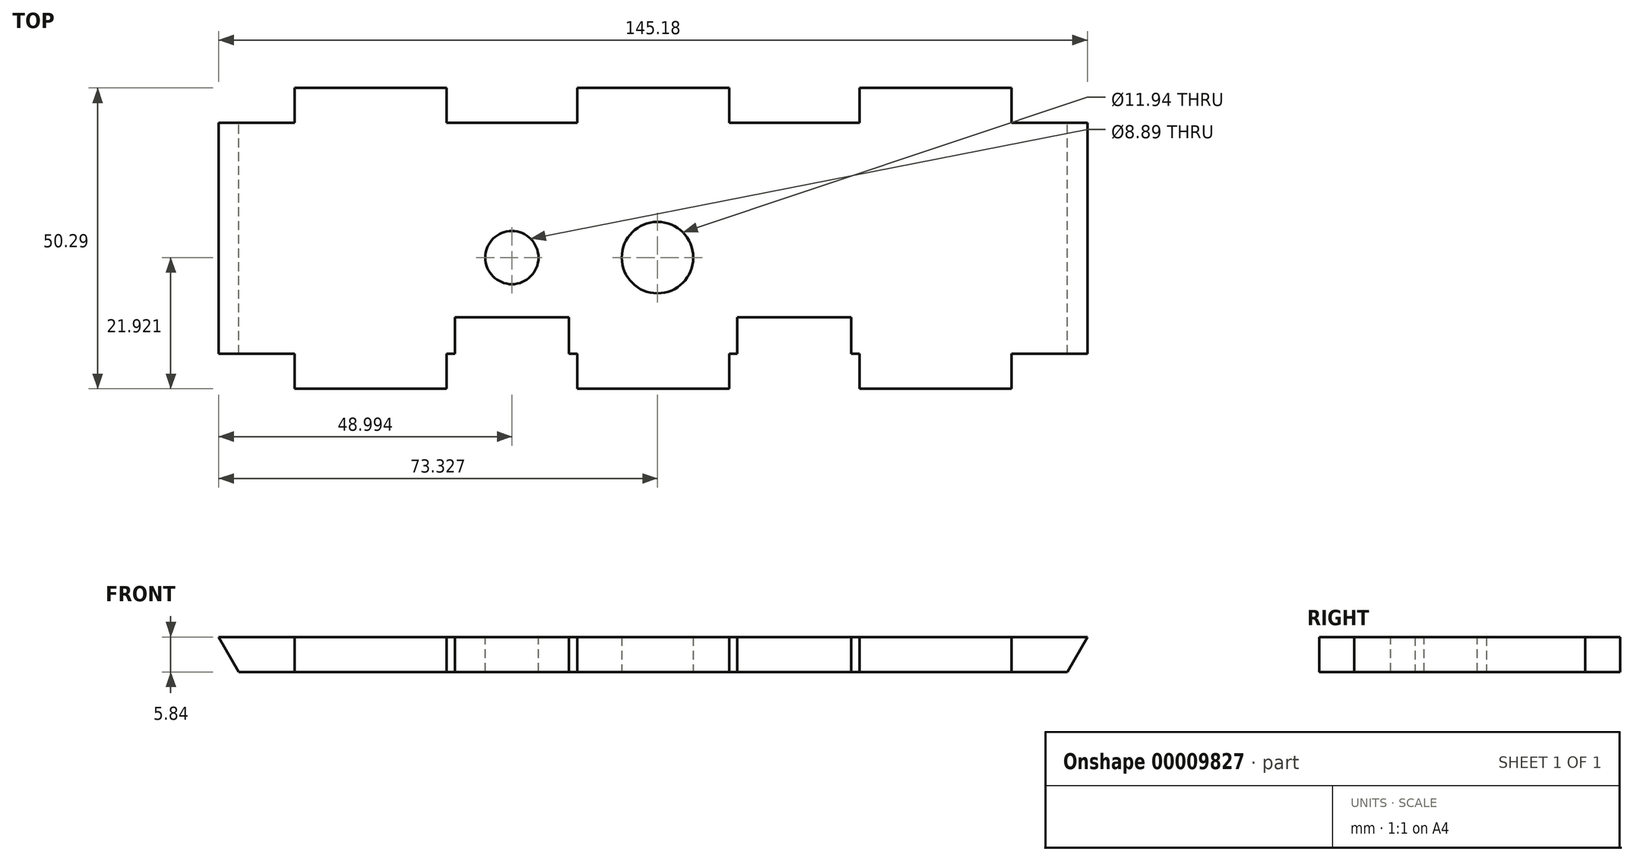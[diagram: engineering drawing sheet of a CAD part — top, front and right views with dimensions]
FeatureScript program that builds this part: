
annotation { "Feature Type Name" : "Feature", "Feature Type Description" : "" }
export const myFeature = defineFeature(function(context is Context, id is Id, definition is map)
    precondition{}
    {
        {
            var Q0;
            Q0=qCreatedBy(makeId("Top.planeOp"),FACE);
            var sketch = newSketch(context, id + "F0", { "sketchPlane" : qUnion([Q0])});
            skLineSegment(sketch, "E0.bottom", {"start": v(-125.55, -7.25) * mm, "end": v(19.63, -7.25) * mm});
            skLineSegment(sketch, "E0.top", {"start": v(-125.55, -57.54) * mm, "end": v(19.63, -57.54) * mm});
            skLineSegment(sketch, "E0.left", {"start": v(-125.55, -7.25) * mm, "end": v(-125.55, -57.54) * mm});
            skLineSegment(sketch, "E0.right", {"start": v(19.63, -7.25) * mm, "end": v(19.63, -57.54) * mm});
            skPoint(sketch, "E1", {"position": v(-52.96, -7.25) * mm});
            skSolve(sketch);
        }
        {
            var Q0;
            Q0=qSketchRegion(id+"F0",true);
            extrude(context, id + "F1", {"entities" : qUnion([Q0]), "depth" : 5.84 * mm});
        }
        {
            var Q0;
            Q0=makeQuery(id+"F1.opExtrude","CAP_FACE",FACE,{"disambiguationData":[OSD([sQuery(id+"F0.wireOp",EDGE,"E0.bottom"),sQuery(id+"F0.wireOp",EDGE,"E0.top"),sQuery(id+"F0.wireOp",EDGE,"E0.left"),sQuery(id+"F0.wireOp",EDGE,"E0.right")])],"isStart":false});
            var sketch = newSketch(context, id + "F2", { "sketchPlane" : qUnion([Q0])});
            skLineSegment(sketch, "E2.bottom", {"start": v(-112.85, -7.25) * mm, "end": v(-87.45, -7.25) * mm});
            skLineSegment(sketch, "E2.left", {"start": v(-112.85, -7.25) * mm, "end": v(-112.85, -13.09) * mm});
            skLineSegment(sketch, "E2.right", {"start": v(-87.45, -7.25) * mm, "end": v(-87.45, -13.09) * mm});
            skLineSegment(sketch, "E3.bottom", {"start": v(-65.66, -7.25) * mm, "end": v(-40.26, -7.25) * mm});
            skLineSegment(sketch, "E3.left", {"start": v(-65.66, -7.25) * mm, "end": v(-65.66, -13.09) * mm});
            skLineSegment(sketch, "E3.right", {"start": v(-40.26, -7.25) * mm, "end": v(-40.26, -13.09) * mm});
            skLineSegment(sketch, "E4.bottom", {"start": v(-18.47, -7.25) * mm, "end": v(6.93, -7.25) * mm});
            skLineSegment(sketch, "E4.left", {"start": v(-18.47, -7.25) * mm, "end": v(-18.47, -13.09) * mm});
            skLineSegment(sketch, "E4.right", {"start": v(6.93, -7.25) * mm, "end": v(6.93, -13.09) * mm});
            skLineSegment(sketch, "E5.bottom", {"start": v(-112.85, -57.54) * mm, "end": v(-87.45, -57.54) * mm});
            skLineSegment(sketch, "E5.left", {"start": v(-112.85, -57.54) * mm, "end": v(-112.85, -51.7) * mm});
            skLineSegment(sketch, "E5.right", {"start": v(-87.45, -57.54) * mm, "end": v(-87.45, -51.7) * mm});
            skLineSegment(sketch, "E6.bottom", {"start": v(-65.66, -57.54) * mm, "end": v(-40.26, -57.54) * mm});
            skLineSegment(sketch, "E6.left", {"start": v(-65.66, -57.54) * mm, "end": v(-65.66, -51.7) * mm});
            skLineSegment(sketch, "E6.right", {"start": v(-40.26, -57.54) * mm, "end": v(-40.26, -51.7) * mm});
            skLineSegment(sketch, "E7.bottom", {"start": v(-18.47, -57.54) * mm, "end": v(6.93, -57.54) * mm});
            skLineSegment(sketch, "E7.left", {"start": v(-18.47, -57.54) * mm, "end": v(-18.47, -51.7) * mm});
            skLineSegment(sketch, "E7.right", {"start": v(6.93, -57.54) * mm, "end": v(6.93, -51.7) * mm});
            skPoint(sketch, "E8", {"position": v(-52.96, -7.25) * mm});
            skPoint(sketch, "E9", {"position": v(-52.96, -57.54) * mm});
            skLineSegment(sketch, "E10", {"start": v(-112.85, -13.09) * mm, "end": v(-125.55, -13.09) * mm});
            skLineSegment(sketch, "E11", {"start": v(-112.85, -51.7) * mm, "end": v(-125.55, -51.7) * mm});
            skLineSegment(sketch, "E12", {"start": v(-125.55, -51.7) * mm, "end": v(-125.55, -13.09) * mm});
            skLineSegment(sketch, "E13", {"start": v(6.93, -13.09) * mm, "end": v(19.63, -13.09) * mm});
            skLineSegment(sketch, "E14", {"start": v(6.93, -51.7) * mm, "end": v(19.63, -51.7) * mm});
            skLineSegment(sketch, "E15", {"start": v(19.63, -51.7) * mm, "end": v(19.63, -13.09) * mm});
            skLineSegment(sketch, "E16", {"start": v(-87.45, -13.09) * mm, "end": v(-65.66, -13.09) * mm});
            skLineSegment(sketch, "E17", {"start": v(-40.26, -13.09) * mm, "end": v(-18.47, -13.09) * mm});
            skLineSegment(sketch, "E18", {"start": v(-18.47, -51.7) * mm, "end": v(-40.26, -51.7) * mm});
            skLineSegment(sketch, "E19", {"start": v(-65.66, -51.7) * mm, "end": v(-87.45, -51.7) * mm});
            skSolve(sketch);
        }
        {
            var Q0;
            {var subQ4=sQuery(id+"F2.wireOp",EDGE,"E2.left");Q0=makeQuery(id+"F2.imprint","IMPRINT",FACE,{"disambiguationData":[TD([[makeQuery(id+"F2.imprint","IMPRINT",EDGE,{"derivedFrom":subQ4}),-1.0]])]});}
            var Q1;
            {var subQ2=sQuery(id+"F2.wireOp",EDGE,"E2.right");Q1=makeQuery(id+"F2.imprint","IMPRINT",FACE,{"disambiguationData":[TD([[makeQuery(id+"F2.imprint","IMPRINT",EDGE,{"derivedFrom":subQ2}),1.0]])]});}
            var Q2;
            {var subQ2=sQuery(id+"F2.wireOp",EDGE,"E3.right");Q2=makeQuery(id+"F2.imprint","IMPRINT",FACE,{"disambiguationData":[TD([[makeQuery(id+"F2.imprint","IMPRINT",EDGE,{"derivedFrom":subQ2}),1.0]])]});}
            var Q3;
            {var subQ4=sQuery(id+"F2.wireOp",EDGE,"E4.right");Q3=makeQuery(id+"F2.imprint","IMPRINT",FACE,{"disambiguationData":[TD([[makeQuery(id+"F2.imprint","IMPRINT",EDGE,{"derivedFrom":subQ4}),1.0]])]});}
            var Q4;
            {var subQ4=sQuery(id+"F2.wireOp",EDGE,"E7.right");Q4=makeQuery(id+"F2.imprint","IMPRINT",FACE,{"disambiguationData":[TD([[makeQuery(id+"F2.imprint","IMPRINT",EDGE,{"derivedFrom":subQ4}),-1.0]])]});}
            var Q5;
            {var subQ2=sQuery(id+"F2.wireOp",EDGE,"E6.right");Q5=makeQuery(id+"F2.imprint","IMPRINT",FACE,{"disambiguationData":[TD([[makeQuery(id+"F2.imprint","IMPRINT",EDGE,{"derivedFrom":subQ2}),-1.0]])]});}
            var Q6;
            {var subQ2=sQuery(id+"F2.wireOp",EDGE,"E5.right");Q6=makeQuery(id+"F2.imprint","IMPRINT",FACE,{"disambiguationData":[TD([[makeQuery(id+"F2.imprint","IMPRINT",EDGE,{"derivedFrom":subQ2}),-1.0]])]});}
            var Q7;
            {var subQ4=sQuery(id+"F2.wireOp",EDGE,"E5.left");Q7=makeQuery(id+"F2.imprint","IMPRINT",FACE,{"disambiguationData":[TD([[makeQuery(id+"F2.imprint","IMPRINT",EDGE,{"derivedFrom":subQ4}),1.0]])]});}
            var Q8;
            Q8=makeQuery(id+"F1.opExtrude","CAP_FACE",FACE,{"disambiguationData":[OSD([sQuery(id+"F0.wireOp",EDGE,"E0.bottom"),sQuery(id+"F0.wireOp",EDGE,"E0.top"),sQuery(id+"F0.wireOp",EDGE,"E0.left"),sQuery(id+"F0.wireOp",EDGE,"E0.right")])],"isStart":false});
            extrude(context, id + "F3", {"entities" : qUnion([Q0, Q1, Q2, Q3, Q4, Q5, Q6, Q7]), "operationType" : NewBodyOperationType.REMOVE, "endBound" : BoundingType.THROUGH_ALL, "oppositeDirection" : true, "endBoundEntityFace" : qUnion([Q8]), "depth" : 25.4 * mm});
        }
        {
            var Q0;
            Q0=makeQuery(id+"F1.opExtrude","CAP_FACE",FACE,{"disambiguationData":[OSD([sQuery(id+"F0.wireOp",EDGE,"E0.bottom"),sQuery(id+"F0.wireOp",EDGE,"E0.top"),sQuery(id+"F0.wireOp",EDGE,"E0.left"),sQuery(id+"F0.wireOp",EDGE,"E0.right")])],"isStart":true});
            var sketch = newSketch(context, id + "F4", { "sketchPlane" : qUnion([Q0])});
            skCircle(sketch, "E20", {"center": v(-52.22, 35.62) * mm, "radius": 5.97 * mm});
            skSolve(sketch);
        }
        {
            var Q0;
            Q0=makeQuery(id+"F4.imprint","IMPRINT",FACE,{"disambiguationData":[TD([[makeQuery(id+"F4.imprint","IMPRINT",EDGE,{"derivedFrom":sQuery(id+"F4.wireOp",EDGE,"E20")}),1.0]])]});
            extrude(context, id + "F5", {"entities" : qUnion([Q0]), "operationType" : NewBodyOperationType.REMOVE, "endBound" : BoundingType.THROUGH_ALL, "oppositeDirection" : true, "depth" : 25.4 * mm});
        }
        {
            var Q0;
            Q0=makeQuery(id+"F1.opExtrude","CAP_FACE",FACE,{"disambiguationData":[OSD([sQuery(id+"F0.wireOp",EDGE,"E0.bottom"),sQuery(id+"F0.wireOp",EDGE,"E0.top"),sQuery(id+"F0.wireOp",EDGE,"E0.left"),sQuery(id+"F0.wireOp",EDGE,"E0.right")])],"isStart":false});
            var sketch = newSketch(context, id + "F6", { "sketchPlane" : qUnion([Q0])});
            skLineSegment(sketch, "E21.bottom", {"start": v(-86.08, -45.6) * mm, "end": v(-67.03, -45.6) * mm});
            skLineSegment(sketch, "E21.top", {"start": v(-86.08, -51.7) * mm, "end": v(-67.03, -51.7) * mm});
            skLineSegment(sketch, "E21.left", {"start": v(-86.08, -45.6) * mm, "end": v(-86.08, -51.7) * mm});
            skLineSegment(sketch, "E21.right", {"start": v(-67.03, -45.6) * mm, "end": v(-67.03, -51.7) * mm});
            skPoint(sketch, "E22", {"position": v(-76.56, -45.6) * mm});
            skLineSegment(sketch, "E23.bottom", {"start": v(-38.89, -45.6) * mm, "end": v(-19.84, -45.6) * mm});
            skLineSegment(sketch, "E23.top", {"start": v(-38.89, -51.7) * mm, "end": v(-19.84, -51.7) * mm});
            skLineSegment(sketch, "E23.left", {"start": v(-38.89, -45.6) * mm, "end": v(-38.89, -51.7) * mm});
            skLineSegment(sketch, "E23.right", {"start": v(-19.84, -45.6) * mm, "end": v(-19.84, -51.7) * mm});
            skPoint(sketch, "E24", {"position": v(-29.36, -51.7) * mm});
            skPoint(sketch, "E25", {"position": v(-76.56, -51.7) * mm});
            skSolve(sketch);
        }
        {
            var Q0;
            Q0=makeQuery(id+"F6.imprint","IMPRINT",FACE,{"disambiguationData":[TD([[makeQuery(id+"F6.imprint","IMPRINT",EDGE,{"derivedFrom":sQuery(id+"F6.wireOp",EDGE,"E21.bottom")}),-1.0]])]});
            var Q1;
            Q1=makeQuery(id+"F6.imprint","IMPRINT",FACE,{"disambiguationData":[TD([[makeQuery(id+"F6.imprint","IMPRINT",EDGE,{"derivedFrom":sQuery(id+"F6.wireOp",EDGE,"E23.bottom")}),-1.0]])]});
            extrude(context, id + "F7", {"entities" : qUnion([Q0, Q1]), "operationType" : NewBodyOperationType.REMOVE, "endBound" : BoundingType.THROUGH_ALL, "oppositeDirection" : true, "depth" : 25.4 * mm});
        }
        {
            var Q0;
            Q0=makeQuery(id+"F3.boolean.opBoolean","COPY",FACE,{"derivedFrom":makeQuery(id+"F3.opExtrude","SWEPT_FACE",FACE,{"disambiguationData":[OSD([sQuery(id+"F2.wireOp",EDGE,"E13")])]})});
            var sketch = newSketch(context, id + "F8", { "sketchPlane" : qUnion([Q0])});
            skLineSegment(sketch, "E26", {"start": v(-19.63, 5.84) * mm, "end": v(-16.26, 0) * mm});
            skLineSegment(sketch, "E27", {"start": v(-16.26, 0) * mm, "end": v(-16.26, 5.84) * mm});
            skLineSegment(sketch, "E28", {"start": v(-16.26, 5.84) * mm, "end": v(-19.63, 5.84) * mm});
            skSolve(sketch);
        }
        {
            var Q0;
            Q0=makeQuery(id+"F3.boolean.opBoolean","COPY",FACE,{"derivedFrom":makeQuery(id+"F3.opExtrude","SWEPT_FACE",FACE,{"disambiguationData":[OSD([sQuery(id+"F2.wireOp",EDGE,"E10")])]})});
            var sketch = newSketch(context, id + "F9", { "sketchPlane" : qUnion([Q0])});
            skLineSegment(sketch, "E29", {"start": v(125.55, 5.84) * mm, "end": v(122.18, 0) * mm});
            skLineSegment(sketch, "E30", {"start": v(122.18, 0) * mm, "end": v(122.18, 5.84) * mm});
            skLineSegment(sketch, "E31", {"start": v(122.18, 5.84) * mm, "end": v(125.55, 5.84) * mm});
            skSolve(sketch);
        }
        {
            var Q0;
            {var subQ3=sQuery(id+"F9.wireOp",EDGE,"E29");Q0=makeQuery(id+"F9.imprint","IMPRINT",FACE,{"disambiguationData":[TD([[makeQuery(id+"F9.imprint","IMPRINT",EDGE,{"derivedFrom":subQ3}),1.0]])]});}
            var Q1;
            {var subQ3=sQuery(id+"F8.wireOp",EDGE,"E26");Q1=makeQuery(id+"F8.imprint","IMPRINT",FACE,{"disambiguationData":[TD([[makeQuery(id+"F8.imprint","IMPRINT",EDGE,{"derivedFrom":subQ3}),-1.0]])]});}
            extrude(context, id + "F10", {"entities" : qUnion([Q0, Q1]), "operationType" : NewBodyOperationType.REMOVE, "endBound" : BoundingType.THROUGH_ALL, "oppositeDirection" : true, "depth" : 25.4 * mm});
        }
        {
            var Q0;
            Q0=makeQuery(id+"F1.opExtrude","CAP_FACE",FACE,{"disambiguationData":[OSD([sQuery(id+"F0.wireOp",EDGE,"E0.bottom"),sQuery(id+"F0.wireOp",EDGE,"E0.top"),sQuery(id+"F0.wireOp",EDGE,"E0.left"),sQuery(id+"F0.wireOp",EDGE,"E0.right")])],"isStart":false});
            var sketch = newSketch(context, id + "F11", { "sketchPlane" : qUnion([Q0])});
            skCircle(sketch, "E32", {"center": v(-76.56, -35.62) * mm, "radius": 4.45 * mm});
            skPoint(sketch, "E33", {"position": v(-76.56, -13.09) * mm});
            skSolve(sketch);
        }
        {
            var Q0;
            Q0=makeQuery(id+"F11.imprint","IMPRINT",FACE,{"disambiguationData":[TD([[makeQuery(id+"F11.imprint","IMPRINT",EDGE,{"derivedFrom":sQuery(id+"F11.wireOp",EDGE,"E32")}),1.0]])]});
            var Q1;
            Q1=makeQuery(id+"F1.opExtrude","CAP_FACE",FACE,{"disambiguationData":[OSD([sQuery(id+"F0.wireOp",EDGE,"E0.bottom"),sQuery(id+"F0.wireOp",EDGE,"E0.top"),sQuery(id+"F0.wireOp",EDGE,"E0.left"),sQuery(id+"F0.wireOp",EDGE,"E0.right")])],"isStart":true});
            extrude(context, id + "F12", {"entities" : qUnion([Q0]), "operationType" : NewBodyOperationType.REMOVE, "endBound" : BoundingType.UP_TO_SURFACE, "oppositeDirection" : true, "endBoundEntityFace" : qUnion([Q1]), "depth" : 25.4 * mm});
        }
    });
